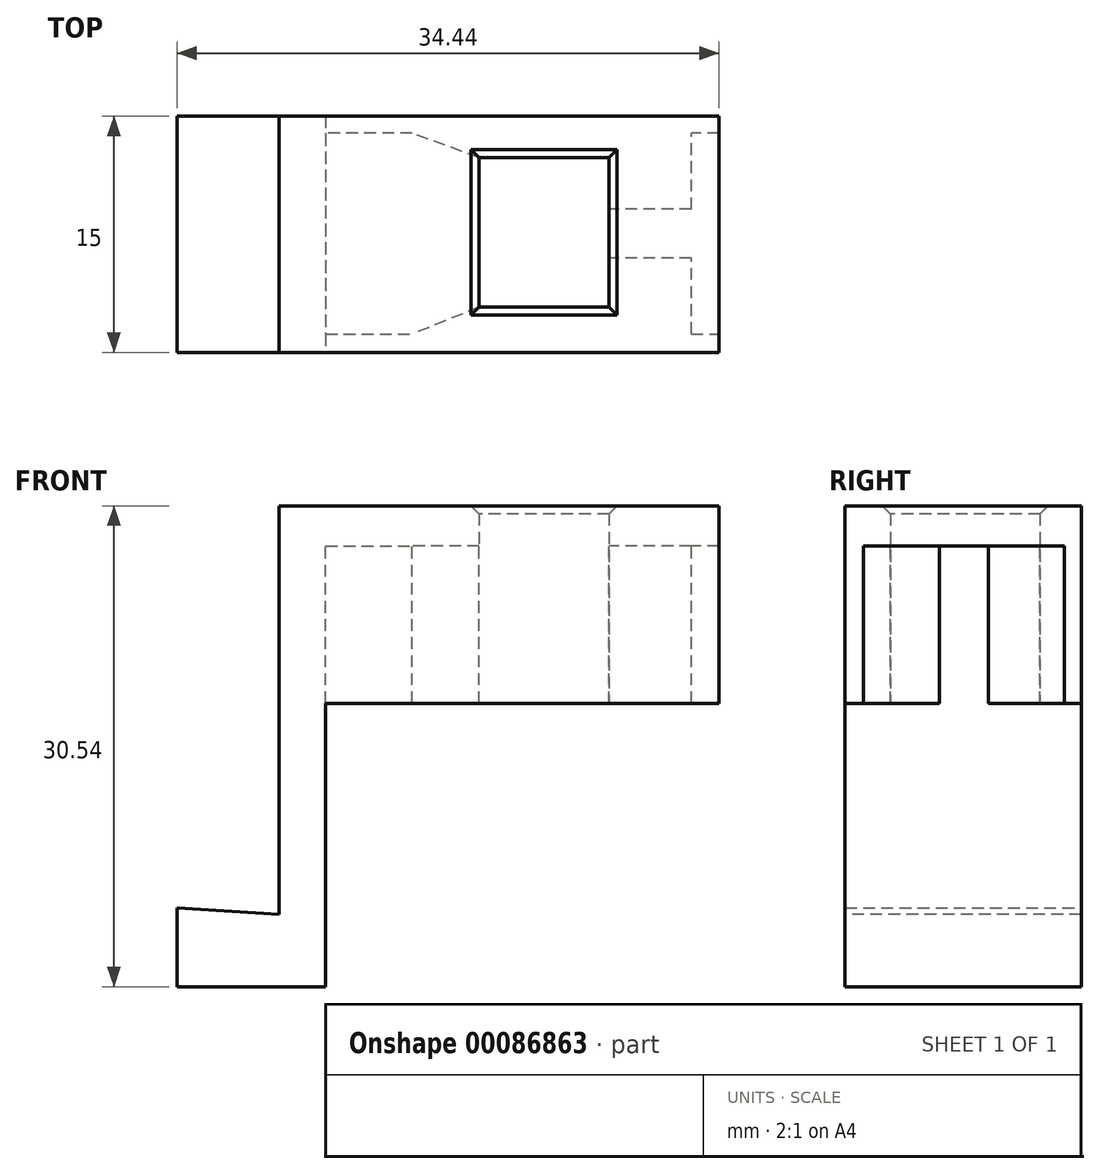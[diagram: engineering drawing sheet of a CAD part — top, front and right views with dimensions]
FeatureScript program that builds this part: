
annotation { "Feature Type Name" : "Feature", "Feature Type Description" : "" }
export const myFeature = defineFeature(function(context is Context, id is Id, definition is map)
    precondition{}
    {
        {
            var Q0;
            Q0=qCreatedBy(makeId("Top.planeOp"),FACE);
            var sketch = newSketch(context, id + "F0", { "sketchPlane" : qUnion([Q0])});
            skLineSegment(sketch, "E0.bottom", {"start": v(-11.23, 11.74) * mm, "end": v(16.71, 11.74) * mm});
            skLineSegment(sketch, "E0.top", {"start": v(-11.23, -3.26) * mm, "end": v(16.71, -3.26) * mm});
            skLineSegment(sketch, "E0.left", {"start": v(-11.23, 11.74) * mm, "end": v(-11.23, -3.26) * mm});
            skLineSegment(sketch, "E0.right", {"start": v(16.71, 11.74) * mm, "end": v(16.71, -3.26) * mm});
            skLineSegment(sketch, "E1.bottom", {"start": v(1.47, 9.12) * mm, "end": v(9.72, 9.12) * mm});
            skLineSegment(sketch, "E1.top", {"start": v(1.47, -0.38) * mm, "end": v(9.72, -0.38) * mm});
            skLineSegment(sketch, "E1.left", {"start": v(1.47, 9.12) * mm, "end": v(1.47, -0.38) * mm});
            skLineSegment(sketch, "E1.right", {"start": v(9.72, 9.12) * mm, "end": v(9.72, -0.38) * mm});
            skSolve(sketch);
        }
        {
            var Q0;
            Q0 = qSketchRegion(id + "F0", true);
            extrude(context, id + "F1", {"entities" : qUnion([Q0]), "depth" : 2.54 * mm});
        }
        {
            var Q0;
            Q0=makeQuery(id+"F1.opExtrude","CAP_FACE",FACE,{"disambiguationData":[OSD([sQuery(id+"F0.wireOp",EDGE,"E0.bottom"),sQuery(id+"F0.wireOp",EDGE,"E0.top"),sQuery(id+"F0.wireOp",EDGE,"E0.left"),sQuery(id+"F0.wireOp",EDGE,"E0.right"),sQuery(id+"F0.wireOp",EDGE,"E1.bottom"),sQuery(id+"F0.wireOp",EDGE,"E1.top"),sQuery(id+"F0.wireOp",EDGE,"E1.left"),sQuery(id+"F0.wireOp",EDGE,"E1.right")])],"isStart":true});
            var sketch = newSketch(context, id + "F2", { "sketchPlane" : qUnion([Q0])});
            skLineSegment(sketch, "E2.bottom", {"start": v(16.71, -11.74) * mm, "end": v(-11.23, -11.74) * mm});
            skLineSegment(sketch, "E2.top", {"start": v(16.71, -10.65) * mm, "end": v(-11.23, -10.65) * mm});
            skLineSegment(sketch, "E2.left", {"start": v(16.71, -11.74) * mm, "end": v(16.71, -10.65) * mm});
            skLineSegment(sketch, "E2.right", {"start": v(-11.23, -11.74) * mm, "end": v(-11.23, -10.65) * mm});
            skLineSegment(sketch, "E3.top", {"start": v(-11.23, 3.26) * mm, "end": v(-8.29, 3.26) * mm});
            skLineSegment(sketch, "E3.left", {"start": v(-11.23, -10.65) * mm, "end": v(-11.23, 3.26) * mm});
            skLineSegment(sketch, "E3.right", {"start": v(-8.29, -10.66) * mm, "end": v(-8.29, 3.26) * mm});
            skLineSegment(sketch, "E4.bottom", {"start": v(-8.29, 3.26) * mm, "end": v(16.71, 3.26) * mm});
            skLineSegment(sketch, "E4.top", {"start": v(-8.29, 2.1) * mm, "end": v(16.71, 2.1) * mm});
            skLineSegment(sketch, "E4.left", {"start": v(-8.29, 3.26) * mm, "end": v(-8.29, 2.1) * mm});
            skLineSegment(sketch, "E4.right", {"start": v(16.71, 3.26) * mm, "end": v(16.71, 2.1) * mm});
            skLineSegment(sketch, "E5.bottom", {"start": v(16.71, 2.1) * mm, "end": v(14.95, 2.1) * mm});
            skLineSegment(sketch, "E5.top", {"start": v(16.71, -10.65) * mm, "end": v(14.95, -10.65) * mm});
            skLineSegment(sketch, "E5.left", {"start": v(16.71, 2.1) * mm, "end": v(16.71, -10.65) * mm});
            skLineSegment(sketch, "E5.right", {"start": v(14.95, 2.1) * mm, "end": v(14.95, -10.65) * mm});
            skLineSegment(sketch, "E6.bottom", {"start": v(9.72, -9.12) * mm, "end": v(1.47, -9.12) * mm});
            skLineSegment(sketch, "E6.top", {"start": v(9.72, 0.38) * mm, "end": v(1.47, 0.38) * mm});
            skLineSegment(sketch, "E6.left", {"start": v(9.72, -9.12) * mm, "end": v(9.72, 0.38) * mm});
            skLineSegment(sketch, "E6.right", {"start": v(1.47, -9.12) * mm, "end": v(1.47, 0.38) * mm});
            skLineSegment(sketch, "E7.bottom", {"start": v(13.63, -10.65) * mm, "end": v(-2.78, -10.65) * mm});
            skLineSegment(sketch, "E7.top", {"start": v(13.63, 2.1) * mm, "end": v(-2.78, 2.1) * mm});
            skLineSegment(sketch, "E7.left", {"start": v(13.63, -10.65) * mm, "end": v(13.63, 2.1) * mm});
            skLineSegment(sketch, "E8", {"start": v(14.95, -2.73) * mm, "end": v(16.71, -2.73) * mm});
            skLineSegment(sketch, "E9", {"start": v(14.95, -5.83) * mm, "end": v(16.71, -5.83) * mm});
            skPoint(sketch, "E10.centerSnap0", {"position": v(-11.23, -4.24) * mm});
            skLineSegment(sketch, "E11", {"start": v(13.63, -2.73) * mm, "end": v(9.72, -2.73) * mm});
            skLineSegment(sketch, "E12", {"start": v(13.63, -5.83) * mm, "end": v(9.72, -5.83) * mm});
            skLineSegment(sketch, "E13", {"start": v(1.47, 0.38) * mm, "end": v(-2.78, 2.1) * mm});
            skLineSegment(sketch, "E14", {"start": v(1.47, -9.12) * mm, "end": v(-2.78, -10.65) * mm});
            skLineSegment(sketch, "E15", {"start": v(13.63, -5.83) * mm, "end": v(14.95, -5.83) * mm});
            skLineSegment(sketch, "E16", {"start": v(14.95, -2.73) * mm, "end": v(13.63, -2.73) * mm});
            skSolve(sketch);
        }
        {
            var Q0;
            Q0=makeQuery(id+"F2.imprint","IMPRINT",FACE,{"disambiguationData":[TD([[makeQuery(id+"F2.imprint","IMPRINT",EDGE,{"derivedFrom":sQuery(id+"F2.wireOp",EDGE,"E3.bottom")}),1.0]])]});
            var Q1;
            Q1=makeQuery(id+"F2.imprint","IMPRINT",FACE,{"disambiguationData":[TD([[makeQuery(id+"F2.imprint","IMPRINT",EDGE,{"derivedFrom":sQuery(id+"F2.wireOp",EDGE,"E2.bottom")}),1.0]])]});
            var Q2;
            {var subQ0=sQuery(id+"F2.wireOp",EDGE,"E5.top");Q2=makeQuery(id+"F2.imprint","IMPRINT",FACE,{"disambiguationData":[TD([[makeQuery(id+"F2.imprint","IMPRINT",EDGE,{"derivedFrom":subQ0}),-1.0]])]});}
            var Q3;
            {var subQ0=sQuery(id+"F2.wireOp",EDGE,"E5.bottom");Q3=makeQuery(id+"F2.imprint","IMPRINT",FACE,{"disambiguationData":[TD([[makeQuery(id+"F2.imprint","IMPRINT",EDGE,{"derivedFrom":subQ0}),1.0]])]});}
            var Q4;
            Q4=makeQuery(id+"F2.imprint","IMPRINT",FACE,{"disambiguationData":[TD([[makeQuery(id+"F2.imprint","IMPRINT",EDGE,{"derivedFrom":sQuery(id+"F2.wireOp",EDGE,"E6.bottom")}),-1.0]])]});
            var Q5;
            Q5=makeQuery(id+"F2.imprint","IMPRINT",FACE,{"disambiguationData":[TD([[makeQuery(id+"F2.imprint","IMPRINT",EDGE,{"derivedFrom":sQuery(id+"F2.wireOp",EDGE,"E4.bottom")}),-1.0]])]});
            var Q6;
            {var subQ4=sQuery(id+"F2.wireOp",EDGE,"E6.top");Q6=makeQuery(id+"F2.imprint","IMPRINT",FACE,{"disambiguationData":[TD([[makeQuery(id+"F2.imprint","IMPRINT",EDGE,{"derivedFrom":subQ4}),1.0]])]});}
            var Q7;
            {var subQ5=sQuery(id+"F2.wireOp",EDGE,"E15");Q7=makeQuery(id+"F2.imprint","IMPRINT",FACE,{"disambiguationData":[TD([[makeQuery(id+"F2.imprint","IMPRINT",EDGE,{"derivedFrom":subQ5}),-1.0]])]});}
            var Q8;
            {var subQ5=sQuery(id+"F2.wireOp",EDGE,"E16");Q8=makeQuery(id+"F2.imprint","IMPRINT",FACE,{"disambiguationData":[TD([[makeQuery(id+"F2.imprint","IMPRINT",EDGE,{"derivedFrom":subQ5}),-1.0]])]});}
            var Q9;
            Q9=makeQuery(id+"F2.imprint","IMPRINT",FACE,{"disambiguationData":[TD([[makeQuery(id+"F2.imprint","IMPRINT",EDGE,{"derivedFrom":sQuery(id+"F2.wireOp",EDGE,"E3.top")}),-1.0]])]});
            extrude(context, id + "F3", {"entities" : qUnion([Q0, Q1, Q2, Q3, Q4, Q5, Q6, Q7, Q8, Q9]), "operationType" : NewBodyOperationType.ADD, "depth" : 10 * mm});
        }
        {
            var Q0;
            Q0=makeQuery(id+"F3.opExtrude","CAP_FACE",FACE,{"disambiguationData":[OSD([sQuery(id+"F2.wireOp",EDGE,"E2.bottom"),sQuery(id+"F2.wireOp",EDGE,"E2.top"),sQuery(id+"F2.wireOp",EDGE,"E2.left"),sQuery(id+"F2.wireOp",EDGE,"E2.right"),sQuery(id+"F2.wireOp",EDGE,"E3.top"),sQuery(id+"F2.wireOp",EDGE,"E3.left"),sQuery(id+"F2.wireOp",EDGE,"E3.right"),sQuery(id+"F2.wireOp",EDGE,"E4.bottom"),sQuery(id+"F2.wireOp",EDGE,"E4.top"),sQuery(id+"F2.wireOp",EDGE,"E4.right"),sQuery(id+"F2.wireOp",EDGE,"E5.left"),sQuery(id+"F2.wireOp",EDGE,"E6.bottom"),sQuery(id+"F2.wireOp",EDGE,"E6.top"),sQuery(id+"F2.wireOp",EDGE,"E6.left"),sQuery(id+"F2.wireOp",EDGE,"E8"),sQuery(id+"F2.wireOp",EDGE,"E9"),sQuery(id+"F2.wireOp",EDGE,"E11"),sQuery(id+"F2.wireOp",EDGE,"E12"),sQuery(id+"F2.wireOp",EDGE,"E13"),sQuery(id+"F2.wireOp",EDGE,"E14"),sQuery(id+"F2.wireOp",EDGE,"E15"),sQuery(id+"F2.wireOp",EDGE,"E16")])],"isStart":false});
            var sketch = newSketch(context, id + "F4", { "sketchPlane" : qUnion([Q0])});
            skLineSegment(sketch, "E17.bottom", {"start": v(-11.23, -11.74) * mm, "end": v(-8.29, -11.74) * mm});
            skLineSegment(sketch, "E17.top", {"start": v(-11.23, 3.26) * mm, "end": v(-8.29, 3.26) * mm});
            skLineSegment(sketch, "E17.left", {"start": v(-11.23, -11.74) * mm, "end": v(-11.23, 3.26) * mm});
            skLineSegment(sketch, "E17.right", {"start": v(-8.29, -11.74) * mm, "end": v(-8.29, 3.26) * mm});
            skSolve(sketch);
        }
        {
            var Q0;
            Q0 = qSketchRegion(id + "F4", true);
            extrude(context, id + "F5", {"entities" : qUnion([Q0]), "operationType" : NewBodyOperationType.ADD, "depth" : 18 * mm});
        }
        {
            var Q0;
            Q0=makeQuery(id+"F5.boolean.opBoolean","MERGE",FACE,{"derivedFrom":[makeQuery(id+"F3.boolean.opBoolean","MERGE",FACE,{"derivedFrom":[makeQuery(id+"F1.opExtrude","SWEPT_FACE",FACE,{"disambiguationData":[OSD([sQuery(id+"F0.wireOp",EDGE,"E0.left")])]}),makeQuery(id+"F3.opExtrude","SWEPT_FACE",FACE,{"disambiguationData":[OSD([sQuery(id+"F2.wireOp",EDGE,"E2.right"),sQuery(id+"F2.wireOp",EDGE,"E3.left")])]})]}),makeQuery(id+"F5.opExtrude","SWEPT_FACE",FACE,{"disambiguationData":[OSD([sQuery(id+"F4.wireOp",EDGE,"E17.left")])]})]});
            var sketch = newSketch(context, id + "F6", { "sketchPlane" : qUnion([Q0])});
            skLineSegment(sketch, "E18.bottom", {"start": v(3.26, -28) * mm, "end": v(-11.74, -28) * mm});
            skLineSegment(sketch, "E18.top", {"start": v(3.26, -23) * mm, "end": v(-11.74, -23) * mm});
            skLineSegment(sketch, "E18.left", {"start": v(3.26, -28) * mm, "end": v(3.26, -23) * mm});
            skLineSegment(sketch, "E18.right", {"start": v(-11.74, -28) * mm, "end": v(-11.74, -23) * mm});
            skSolve(sketch);
        }
        {
            var Q0;
            Q0 = qSketchRegion(id + "F6", true);
            extrude(context, id + "F7", {"entities" : qUnion([Q0]), "operationType" : NewBodyOperationType.ADD, "depth" : 6.5 * mm});
        }
        {
            var Q0;
            Q0=makeQuery(id+"F7.boolean.opBoolean","MERGE",FACE,{"derivedFrom":[makeQuery(id+"F5.boolean.opBoolean","MERGE",FACE,{"derivedFrom":[makeQuery(id+"F3.boolean.opBoolean","MERGE",FACE,{"derivedFrom":[makeQuery(id+"F1.opExtrude","SWEPT_FACE",FACE,{"disambiguationData":[OSD([sQuery(id+"F0.wireOp",EDGE,"E0.top")])]}),makeQuery(id+"F3.opExtrude","SWEPT_FACE",FACE,{"disambiguationData":[OSD([sQuery(id+"F2.wireOp",EDGE,"E3.top"),sQuery(id+"F2.wireOp",EDGE,"E4.bottom")])]})]}),makeQuery(id+"F5.opExtrude","SWEPT_FACE",FACE,{"disambiguationData":[OSD([sQuery(id+"F4.wireOp",EDGE,"E17.top")])]})]}),makeQuery(id+"F7.opExtrude","SWEPT_FACE",FACE,{"disambiguationData":[OSD([sQuery(id+"F6.wireOp",EDGE,"E18.left")])]})]});
            var sketch = newSketch(context, id + "F8", { "sketchPlane" : qUnion([Q0])});
            skLineSegment(sketch, "E19", {"start": v(-17.73, -23) * mm, "end": v(-11.23, -23.4) * mm});
            skLineSegment(sketch, "E20", {"start": v(-11.23, -23) * mm, "end": v(-11.23, -23.4) * mm});
            skSolve(sketch);
        }
        {
            var Q0;
            Q0=makeQuery(id+"F8.imprint","IMPRINT",FACE,{"disambiguationData":[TD([[makeQuery(id+"F8.imprint","IMPRINT",EDGE,{"derivedFrom":sQuery(id+"F8.wireOp",EDGE,"E19")}),1.0]])]});
            extrude(context, id + "F9", {"entities" : qUnion([Q0]), "operationType" : NewBodyOperationType.REMOVE, "oppositeDirection" : true, "depth" : 25.4 * mm});
        }
        {
            var Q0;
            Q0=makeQuery(id+"F1.opExtrude","CAP_EDGE",EDGE,{"disambiguationData":[OSD([sQuery(id+"F0.wireOp",EDGE,"E1.left")])],"isStart":false});
            var Q1;
            Q1=makeQuery(id+"F1.opExtrude","CAP_EDGE",EDGE,{"disambiguationData":[OSD([sQuery(id+"F0.wireOp",EDGE,"E1.bottom")])],"isStart":false});
            var Q2;
            Q2=makeQuery(id+"F1.opExtrude","CAP_EDGE",EDGE,{"disambiguationData":[OSD([sQuery(id+"F0.wireOp",EDGE,"E1.right")])],"isStart":false});
            var Q3;
            Q3=makeQuery(id+"F1.opExtrude","CAP_EDGE",EDGE,{"disambiguationData":[OSD([sQuery(id+"F0.wireOp",EDGE,"E1.top")])],"isStart":false});
            chamfer(context, id + "F10", {"entities" : qUnion([Q0, Q1, Q2, Q3]), "width" : 0.5 * mm, "tangentPropagation" : true});
        }
    });
